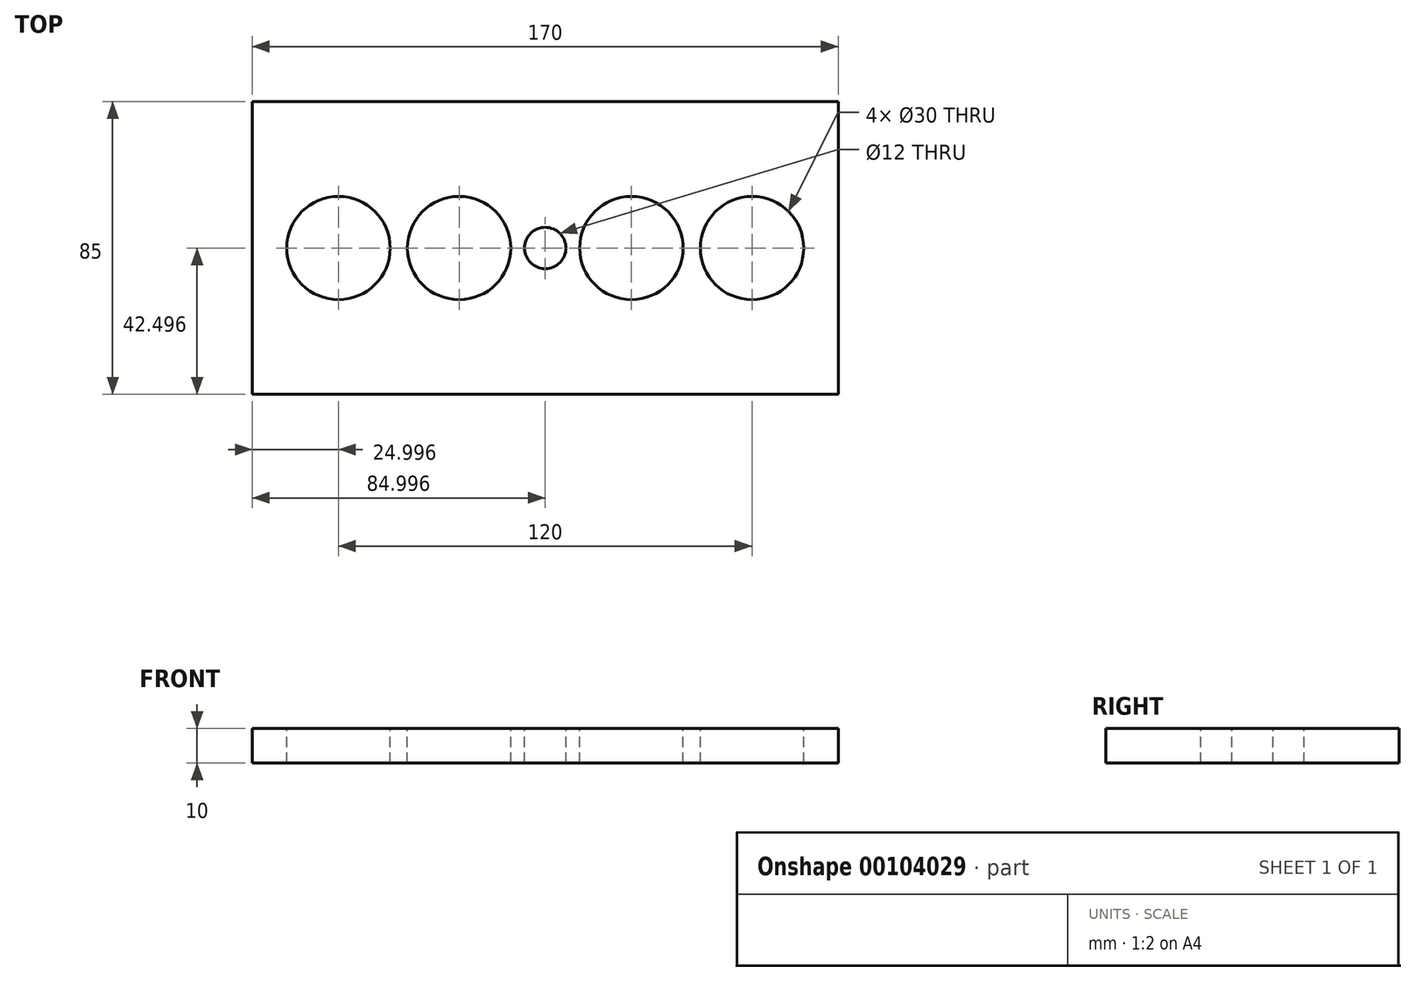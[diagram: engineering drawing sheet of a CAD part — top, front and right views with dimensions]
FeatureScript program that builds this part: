
annotation { "Feature Type Name" : "Feature", "Feature Type Description" : "" }
export const myFeature = defineFeature(function(context is Context, id is Id, definition is map)
    precondition{}
    {
        {
            var Q0;
            Q0=qCreatedBy(makeId("Top.planeOp"),FACE);
            var sketch = newSketch(context, id + "F0", { "sketchPlane" : qUnion([Q0])});
            skLineSegment(sketch, "E0.bottom", {"start": v(-86.72, 37.98) * mm, "end": v(83.28, 37.98) * mm});
            skLineSegment(sketch, "E0.top", {"start": v(-86.72, -47.02) * mm, "end": v(83.28, -47.02) * mm});
            skLineSegment(sketch, "E0.left", {"start": v(-86.72, 37.98) * mm, "end": v(-86.72, -47.02) * mm});
            skLineSegment(sketch, "E0.right", {"start": v(83.28, 37.98) * mm, "end": v(83.28, -47.02) * mm});
            skSolve(sketch);
        }
        {
            var Q0;
            Q0=makeQuery(id+"F0.imprint","IMPRINT",FACE,{"disambiguationData":[TD([[makeQuery(id+"F0.imprint","IMPRINT",EDGE,{"derivedFrom":sQuery(id+"F0.wireOp",EDGE,"E0.bottom")}),-1.0]])]});
            extrude(context, id + "F1", {"entities" : qUnion([Q0]), "depth" : 10 * mm, "offsetDistance" : 25 * mm});
        }
        {
            var Q0;
            Q0=makeQuery(id+"F1.opExtrude","CAP_FACE",FACE,{"disambiguationData":[OSD([sQuery(id+"F0.wireOp",EDGE,"E0.bottom"),sQuery(id+"F0.wireOp",EDGE,"E0.top"),sQuery(id+"F0.wireOp",EDGE,"E0.left"),sQuery(id+"F0.wireOp",EDGE,"E0.right")])],"isStart":false});
            var sketch = newSketch(context, id + "F2", { "sketchPlane" : qUnion([Q0])});
            skCircle(sketch, "E1", {"center": v(-61.72, -4.52) * mm, "radius": 15 * mm});
            skPoint(sketch, "E1.centerSnap0", {"position": v(-86.72, -4.52) * mm});
            skCircle(sketch, "E2", {"center": v(-26.72, -4.52) * mm, "radius": 15 * mm});
            skCircle(sketch, "E3", {"center": v(-1.72, -4.52) * mm, "radius": 6 * mm});
            skCircle(sketch, "E4", {"center": v(23.28, -4.52) * mm, "radius": 15 * mm});
            skCircle(sketch, "E5", {"center": v(58.28, -4.52) * mm, "radius": 15 * mm});
            skPoint(sketch, "E6", {"position": v(-1.72, 37.98) * mm});
            skSolve(sketch);
        }
        {
            var Q0;
            Q0 = qSketchRegion(id + "F2", true);
            extrude(context, id + "F3", {"entities" : qUnion([Q0]), "operationType" : NewBodyOperationType.REMOVE, "endBound" : BoundingType.THROUGH_ALL, "oppositeDirection" : true, "depth" : 25 * mm, "offsetDistance" : 25 * mm});
        }
    });
